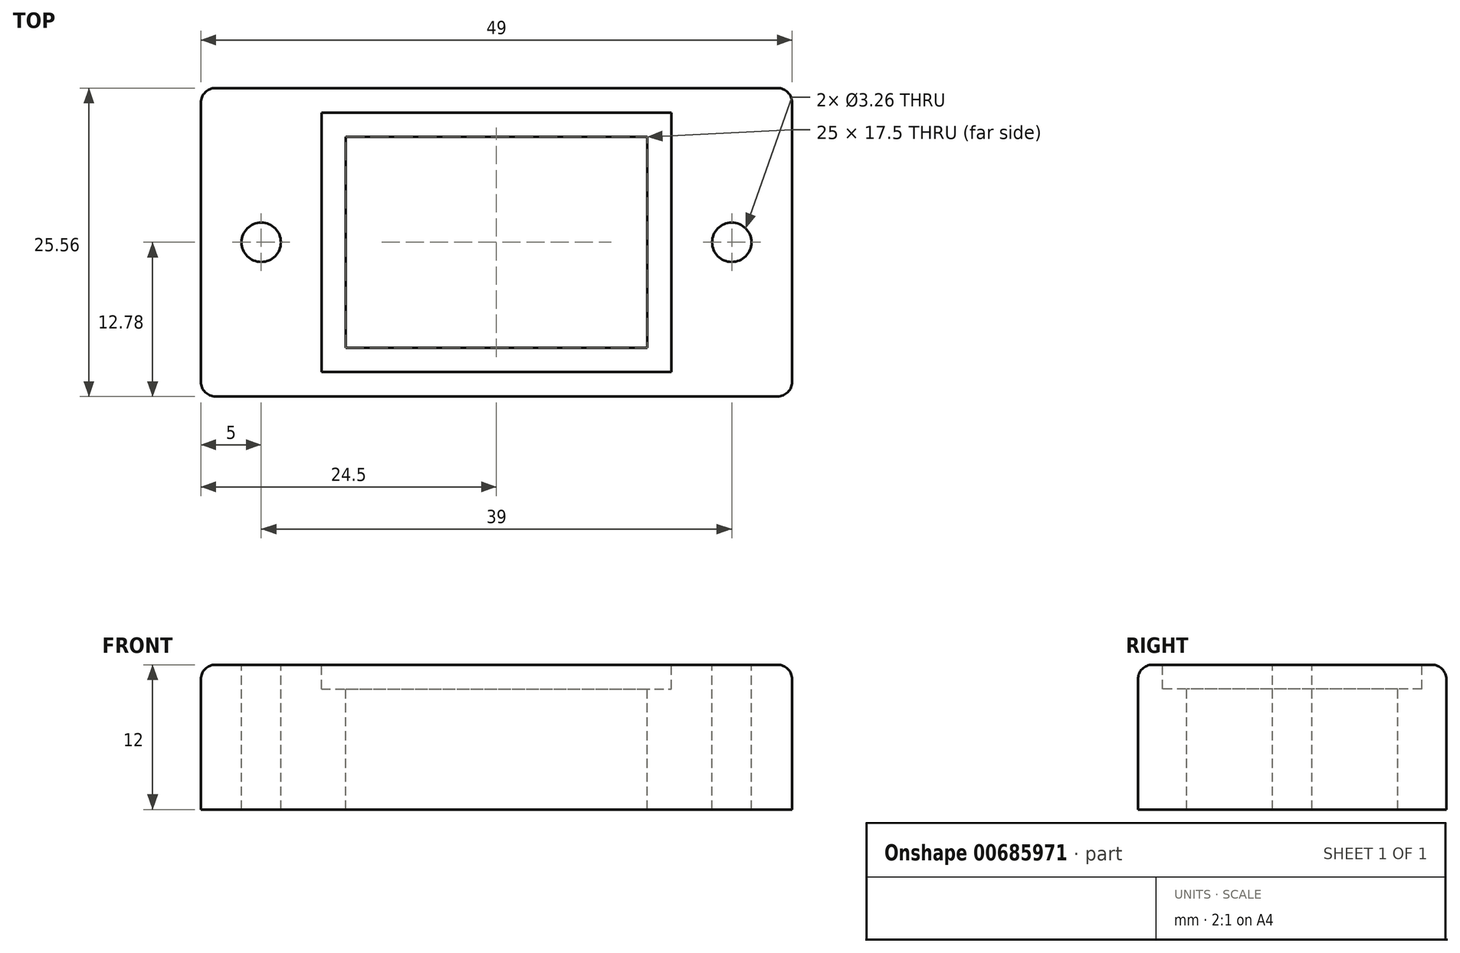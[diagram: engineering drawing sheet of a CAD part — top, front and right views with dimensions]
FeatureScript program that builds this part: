
annotation { "Feature Type Name" : "Feature", "Feature Type Description" : "" }
export const myFeature = defineFeature(function(context is Context, id is Id, definition is map)
    precondition{}
    {
        {
            var Q0;
            Q0=qCreatedBy(makeId("Top.planeOp"),FACE);
            var sketch = newSketch(context, id + "F0", { "sketchPlane" : qUnion([Q0])});
            skLineSegment(sketch, "E0.bottom", {"start": v(-24.5, 12.78) * mm, "end": v(24.5, 12.78) * mm});
            skLineSegment(sketch, "E0.top", {"start": v(-24.5, -12.78) * mm, "end": v(24.5, -12.78) * mm});
            skLineSegment(sketch, "E0.left", {"start": v(-24.5, 12.78) * mm, "end": v(-24.5, -12.78) * mm});
            skLineSegment(sketch, "E0.right", {"start": v(24.5, 12.78) * mm, "end": v(24.5, -12.78) * mm});
            skPoint(sketch, "E0.middle", {"position": v(0, 0) * mm});
            skSolve(sketch);
        }
        {
            var Q0;
            Q0 = qSketchRegion(id + "F2", true);
            var Q1;
            Q1=makeQuery(id+"F0.imprint","IMPRINT",FACE,{"disambiguationData":[TD([[makeQuery(id+"F0.imprint","IMPRINT",EDGE,{"derivedFrom":sQuery(id+"F0.wireOp",EDGE,"E0.bottom")}),-1.0]])]});
            extrude(context, id + "F1", {"entities" : qUnion([Q0, Q1]), "oppositeDirection" : true, "depth" : 12 * mm, "offsetDistance" : 25 * mm});
        }
        {
            var Q0;
            Q0=makeQuery(id+"F1.opExtrude","CAP_FACE",FACE,{"disambiguationData":[OSD([sQuery(id+"F0.wireOp",EDGE,"E0.bottom"),sQuery(id+"F0.wireOp",EDGE,"E0.top"),sQuery(id+"F0.wireOp",EDGE,"E0.left"),sQuery(id+"F0.wireOp",EDGE,"E0.right")])],"isStart":true});
            var sketch = newSketch(context, id + "F2", { "sketchPlane" : qUnion([Q0])});
            skLineSegment(sketch, "E1.bottom", {"start": v(-14.5, 10.75) * mm, "end": v(14.5, 10.75) * mm});
            skLineSegment(sketch, "E1.top", {"start": v(-14.5, -10.75) * mm, "end": v(14.5, -10.75) * mm});
            skLineSegment(sketch, "E1.left", {"start": v(-14.5, 10.75) * mm, "end": v(-14.5, -10.75) * mm});
            skLineSegment(sketch, "E1.right", {"start": v(14.5, 10.75) * mm, "end": v(14.5, -10.75) * mm});
            skPoint(sketch, "E1.middle", {"position": v(0, 0) * mm});
            skSolve(sketch);
        }
        {
            var Q0;
            Q0=makeQuery(id+"F2.imprint","IMPRINT",FACE,{"disambiguationData":[TD([[makeQuery(id+"F2.imprint","IMPRINT",EDGE,{"derivedFrom":sQuery(id+"F2.wireOp",EDGE,"E1.bottom")}),-1.0]])]});
            var Q1;
            Q1=sQuery(id+"F2.wireOp",EDGE,"E1.left");
            var Q2;
            Q2=sQuery(id+"F2.wireOp",EDGE,"E1.bottom");
            var Q3;
            Q3=sQuery(id+"F2.wireOp",EDGE,"E1.right");
            var Q4;
            Q4=sQuery(id+"F2.wireOp",EDGE,"E1.top");
            extrude(context, id + "F3", {"entities" : qUnion([Q0]), "operationType" : NewBodyOperationType.REMOVE, "surfaceEntities" : qUnion([Q1, Q2, Q3, Q4]), "oppositeDirection" : true, "depth" : 2 * mm, "offsetDistance" : 25 * mm});
        }
        {
            var Q0;
            Q0=qCreatedBy(makeId("Top.planeOp"),FACE);
            var sketch = newSketch(context, id + "F4", { "sketchPlane" : qUnion([Q0])});
            skLineSegment(sketch, "E2.bottom", {"start": v(-12.5, 8.75) * mm, "end": v(12.5, 8.75) * mm});
            skLineSegment(sketch, "E2.top", {"start": v(-12.5, -8.75) * mm, "end": v(12.5, -8.75) * mm});
            skLineSegment(sketch, "E2.left", {"start": v(-12.5, 8.75) * mm, "end": v(-12.5, -8.75) * mm});
            skLineSegment(sketch, "E2.right", {"start": v(12.5, 8.75) * mm, "end": v(12.5, -8.75) * mm});
            skPoint(sketch, "E2.middle", {"position": v(0, 0) * mm});
            skSolve(sketch);
        }
        {
            var Q0;
            Q0=makeQuery(id+"F4.imprint","IMPRINT",FACE,{"disambiguationData":[TD([[makeQuery(id+"F4.imprint","IMPRINT",EDGE,{"derivedFrom":sQuery(id+"F4.wireOp",EDGE,"E2.bottom")}),-1.0]])]});
            extrude(context, id + "F5", {"entities" : qUnion([Q0]), "operationType" : NewBodyOperationType.REMOVE, "oppositeDirection" : true, "depth" : 12 * mm, "offsetDistance" : 25 * mm});
        }
        {
            var Q0;
            Q0=makeQuery(id+"F1.opExtrude","CAP_FACE",FACE,{"disambiguationData":[OSD([sQuery(id+"F0.wireOp",EDGE,"E0.bottom"),sQuery(id+"F0.wireOp",EDGE,"E0.top"),sQuery(id+"F0.wireOp",EDGE,"E0.left"),sQuery(id+"F0.wireOp",EDGE,"E0.right")])],"isStart":true});
            var sketch = newSketch(context, id + "F6", { "sketchPlane" : qUnion([Q0])});
            skPoint(sketch, "E3", {"position": v(-19.5, 0) * mm});
            skPoint(sketch, "E4", {"position": v(19.5, 0) * mm});
            skSolve(sketch);
        }
        {
            var Q0;
            Q0=sQuery(id+"F6.wireOp",VERTEX,"E3");
            var Q1;
            Q1=sQuery(id+"F6.wireOp",VERTEX,"E4");
            var Q2;
            Q2=makeQuery(id+"F1.opExtrude","SWEPT_BODY",BODY,{"disambiguationData":[OSD([sQuery(id+"F0.wireOp",EDGE,"E0.bottom"),sQuery(id+"F0.wireOp",EDGE,"E0.top"),sQuery(id+"F0.wireOp",EDGE,"E0.left"),sQuery(id+"F0.wireOp",EDGE,"E0.right")])]});
            hole(context, id + "F7", {"style" : HoleStyle.SIMPLE, "endStyle" : HoleEndStyle.THROUGH, "standardTappedOrClearance" : lookupTablePath({ "standard" : "ANSI", "fit" : "Normal (ASME)", "size" : "#4", "type" : "Clearance" }), "standardBlindInLast" : lookupTablePath({ "fit" : "Free", "standard" : "ANSI", "size" : "#4", "type" : "Clearance" }), "holeDiameter" : 3.26 * mm, "majorDiameter" : 5 * mm, "isTappedThrough" : true, "tappedDepth" : 12 * mm, "tapClearance" : 3, "locations" : qUnion([Q0, Q1]), "scope" : qUnion([Q2])});
        }
        {
            var Q0;
            Q0=makeQuery(id+"F1.opExtrude","CAP_EDGE",EDGE,{"disambiguationData":[OSD([sQuery(id+"F0.wireOp",EDGE,"E0.top")])],"isStart":true});
            fillet(context, id + "F8", {"entities" : qUnion([Q0]), "radius" : 1.2 * mm, "tangentPropagation" : true, "allowEdgeOverflow" : false});
        }
        {
            var Q0;
            Q0=makeQuery(id+"F1.opExtrude","CAP_EDGE",EDGE,{"disambiguationData":[OSD([sQuery(id+"F0.wireOp",EDGE,"E0.right")])],"isStart":true});
            fillet(context, id + "F9", {"entities" : qUnion([Q0]), "radius" : 1.2 * mm, "tangentPropagation" : true, "allowEdgeOverflow" : false});
        }
        {
            var Q0;
            Q0=makeQuery(id+"F1.opExtrude","CAP_EDGE",EDGE,{"disambiguationData":[OSD([sQuery(id+"F0.wireOp",EDGE,"E0.left")])],"isStart":true});
            fillet(context, id + "F10", {"entities" : qUnion([Q0]), "radius" : 1.2 * mm, "tangentPropagation" : true, "allowEdgeOverflow" : false});
        }
        {
            var Q0;
            Q0=makeQuery(id+"F1.opExtrude","CAP_EDGE",EDGE,{"disambiguationData":[OSD([sQuery(id+"F0.wireOp",EDGE,"E0.bottom")])],"isStart":true});
            fillet(context, id + "F11", {"entities" : qUnion([Q0]), "radius" : 1.2 * mm, "tangentPropagation" : true, "allowEdgeOverflow" : false});
        }
    });
